# Revit family: DIN-Kreuzverbinder für Flachleiter FT
name_source: partatom
category: Generic Models
revit_build: Autodesk Revit 2015 (Build: 20140606_1530(x64)
units: mm (PartAtom-declared; Revit-internal decimal feet)

## types (2) — shared parameters
Height = 3 mm  [stored 0.00984252 ft]
Height 1 = 2 mm  [stored 0.00656168 ft]
Manufacturer = OBO Bettermann
Material = Steel, Galvanized
URL = http://www.obo-bettermann.com

## per-type parameters (varying)
| type | Article Type | GTIN | Length | Length 1 | Length 2 | Manufacturer Art.No. | Width | Width 1 | Width 2 |
| 256 A-DIN 30 FT | 256 A-DIN 30 FT | 4012195419471 | 60 mm  [stored 0.19685 ft] | 20 mm  [stored 0.0656168 ft] | 14 mm  [stored 0.0459318 ft] | 5314658 | 60 mm  [stored 0.19685 ft] | 20 mm  [stored 0.0656168 ft] | 13 mm |
| 256 A-DIN 40 FT | 256 A-DIN 40 FT

256 A-DIN 40 FT
256 A-DIN 40 FT | 4012195419532 | 80 mm  [stored 0.262467 ft] | 27 mm  [stored 0.0885827 ft] | 21 mm | 5314666

5314666
5314666 | 80 mm  [stored 0.262467 ft] | 27 mm  [stored 0.0885827 ft] | 20 mm  [stored 0.0656168 ft] |

note: [stored X ft] marks values corroborated as IEEE doubles in the binary element streams (Revit-internal decimal feet)

## geometry (parser evidence)
native form markers: Sweep x2
no freeform markers — native parametric forms only
